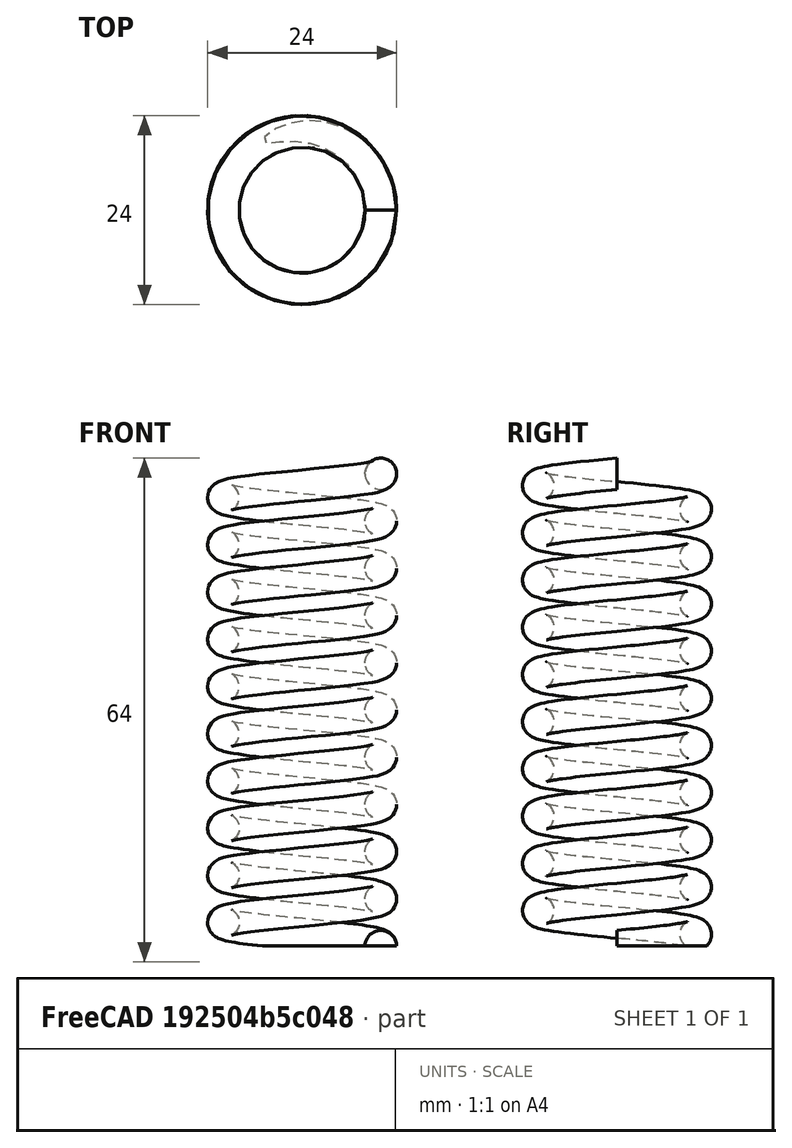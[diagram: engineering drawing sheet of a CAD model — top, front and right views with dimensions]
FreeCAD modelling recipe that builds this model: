
FCSTD DOCUMENT  (FreeCAD 0.16R6700 (Git))
Label: Aula06 - Mola
License: FreeArt
LicenseURL: http://artlibre.org/licence/lal
objects: Part::Helix×1, Sketcher::SketchObject×1, Part::Sweep×1, Part::Box×1, Part::Cut×1
note: 5 computed .brp shape members not serialized (recipe doc carries the construction recipe); baked Part::Feature solids carry a one-line shape summary decoded from their .brp

FEATURE [Part::Helix] Helix
  Angle = 0
  Height = 60
  LocalCoord = 0
  Pitch = 6
  Radius = 10
  Style = 1
FEATURE [Sketcher::SketchObject] Sketch  label="Perfil da Mola"
  Placement = pos=(0,0,0) rot=(-1,0,0;4.71239rad)
  sketch-geometry (1):
    g0: Circle CenterX=10 CenterY=0 CenterZ=0 NormalX=0 NormalY=0 NormalZ=1 Radius=2
  constraints (2):
    c: DistanceX(g-1,g0) = 10
    c: Radius(g0) = 2
FEATURE [Part::Sweep] Sweep
  Frenet = true
  Sections = -> [Sketch]
  Solid = true
  Spine = -> Helix [Edge2,Edge1,Edge3,Edge4,Edge5,Edge6,Edge7,Edge8,Edge9,Edge10]
  Transition = 1
FEATURE [Part::Box] Box  label="Chanfro de Baixo"
  Height = 3
  Length = 25
  Placement = pos=(-312.094,287.885,-299.23) rot=(0,0,1;0rad)
  Width = 25
FEATURE [Part::Cut] Cut
  Base = -> Sweep
  Tool = -> Box
